# Revit family: IP Remote Enclosure
name_source: partatom
category: Electrical Fixtures
revit_build: Autodesk Revit 2015 (Build: 20140606_1530(x64)
units: mm (PartAtom-declared; Revit-internal decimal feet)

## types (2) — shared parameters
Mounting = Surface or Suspension
Operating Mode = Maintained
Operating Voltage = 240VAC 50Hz

## per-type parameters (varying)
| type | Battery | Dimensions | Emergency Driver | Lamp | Main Driver | Output Parameters |
| CLEDDRVM-16V500C | 1550260	    Battery,   LP 6.4V 3200mA 200mm lead SBS | 380mm x 190mm x 110mm | 8002621    PCA:LED PP.Driver.16V 500mA. CT10220-L2
PCA:LED PP.Driver.16V 500mA. CT10220-L2
PCA:LED PP.Driver.16V 500mA. CT10220-L2
8002621    PCA: LED PP, Driver, 16V 500mA |  | 1330060    LED Driver 1-16W, 500mA, 2-32V | Constant Current Drive: 48VDC @ 95mA |
| LWELED-FZR-IPREM | 15300260	    Battery,   LP 3.3V 2500mA 200mm lead SBS | 380mm x 190mm x 130mm | 8002340	      PCA: LWELED Driver | 8002430	      PCA: Duris P5 6LED Strip, L10, #CT10166-D1 |  |  |

## geometry (parser evidence)
native form markers: Sweep x3
no freeform markers — native parametric forms only
